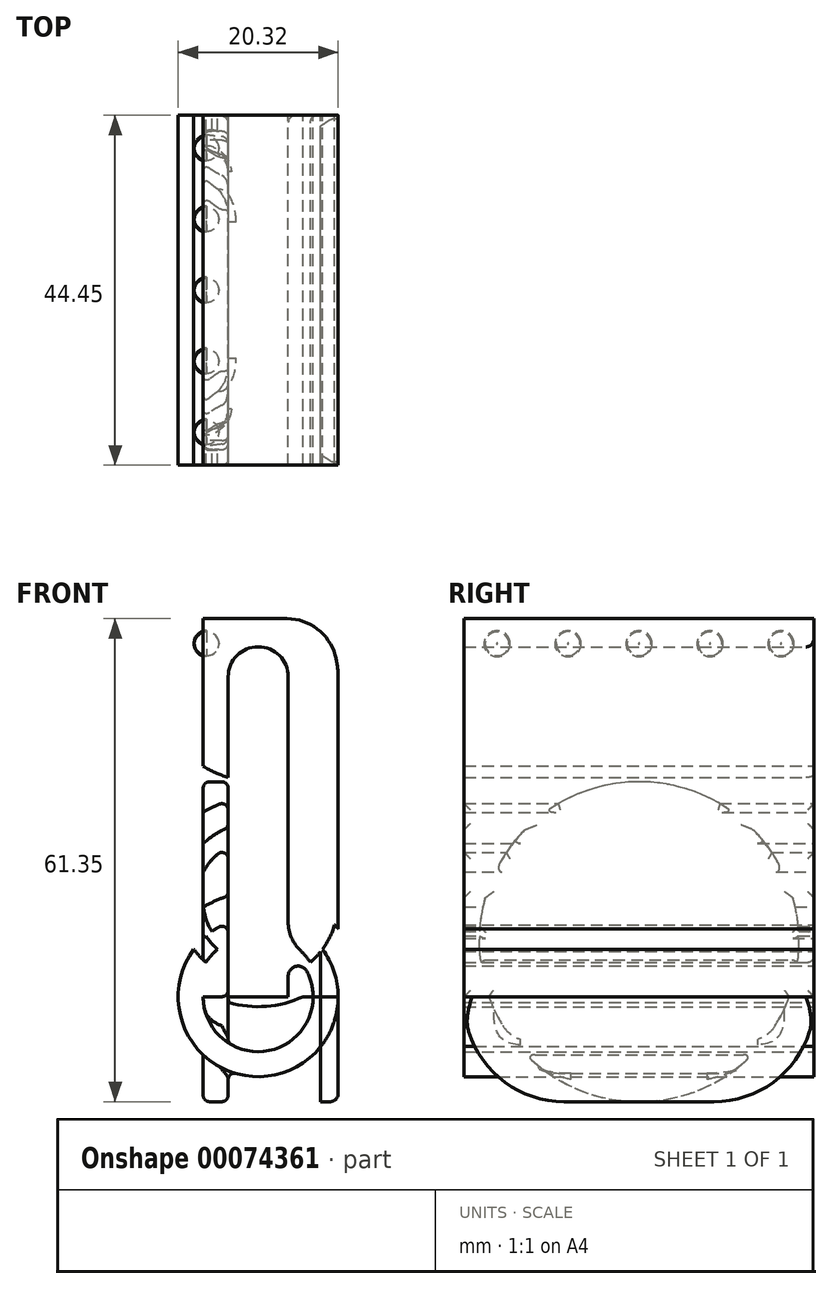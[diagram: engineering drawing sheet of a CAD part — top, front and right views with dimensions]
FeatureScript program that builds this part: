
annotation { "Feature Type Name" : "Feature", "Feature Type Description" : "" }
export const myFeature = defineFeature(function(context is Context, id is Id, definition is map)
    precondition{}
    {
        {
            var Q0;
            Q0=qCreatedBy(makeId("Front.planeOp"),FACE);
            var sketch = newSketch(context, id + "F0", { "sketchPlane" : qUnion([Q0])});
            skCircle(sketch, "E0", {"center": v(0, 0) * mm, "radius": 3.81 * mm});
            skCircle(sketch, "E1", {"center": v(0, -12.07) * mm, "radius": 3.81 * mm});
            skCircle(sketch, "E2", {"center": v(0, 0) * mm, "radius": 6.99 * mm});
            skCircle(sketch, "E3", {"center": v(0, -12.07) * mm, "radius": 6.99 * mm});
            skLineSegment(sketch, "E4", {"start": v(-6.99, -12.06) * mm, "end": v(-6.99, 28.58) * mm});
            skLineSegment(sketch, "E5", {"start": v(0, -12.07) * mm, "end": v(0, 0) * mm, "construction": true});
            skLineSegment(sketch, "E6", {"start": v(0, 0) * mm, "end": v(0, 28.58) * mm, "construction": true});
            skCircle(sketch, "E7", {"center": v(0, 28.58) * mm, "radius": 3.81 * mm});
            skCircle(sketch, "E8", {"center": v(0, 28.58) * mm, "radius": 10.16 * mm});
            skCircle(sketch, "E9", {"center": v(0, 0) * mm, "radius": 13.34 * mm});
            skCircle(sketch, "E10", {"center": v(0, -12.07) * mm, "radius": 13.34 * mm});
            skCircle(sketch, "E11", {"center": v(0, 28.58) * mm, "radius": 6.99 * mm});
            skCircle(sketch, "E12", {"center": v(0, 0) * mm, "radius": 7.94 * mm});
            skCircle(sketch, "E13", {"center": v(0, -12.07) * mm, "radius": 7.94 * mm});
            skCircle(sketch, "E14", {"center": v(0, 0) * mm, "radius": 10.16 * mm});
            skCircle(sketch, "E15", {"center": v(0, -12.07) * mm, "radius": 10.16 * mm});
            skCircle(sketch, "E16", {"center": v(0, 28.58) * mm, "radius": 13.34 * mm});
            skLineSegment(sketch, "E17", {"start": v(10.16, 28.58) * mm, "end": v(10.16, 0) * mm});
            skLineSegment(sketch, "E18", {"start": v(0, -25.4) * mm, "end": v(25.77, -25.4) * mm, "construction": true});
            skLineSegment(sketch, "E19", {"start": v(10.16, 0) * mm, "end": v(10.16, -25.4) * mm});
            skLineSegment(sketch, "E20", {"start": v(7.94, 0) * mm, "end": v(7.94, -25.4) * mm});
            skLineSegment(sketch, "E21", {"start": v(6.99, 28.58) * mm, "end": v(7.94, 0) * mm});
            skLineSegment(sketch, "E22", {"start": v(-6.99, 28.58) * mm, "end": v(10.16, 28.58) * mm});
            skLineSegment(sketch, "E23", {"start": v(-6.99, -12.07) * mm, "end": v(10.16, -12.07) * mm});
            skLineSegment(sketch, "E24", {"start": v(-3.81, 28.58) * mm, "end": v(-3.81, -12.07) * mm});
            skLineSegment(sketch, "E25", {"start": v(3.81, 28.58) * mm, "end": v(3.81, 0) * mm});
            skLineSegment(sketch, "E26", {"start": v(3.81, 0) * mm, "end": v(3.81, -12.07) * mm});
            skPoint(sketch, "E26.endSnap0", {"position": v(1.59, -12.07) * mm});
            skLineSegment(sketch, "E27", {"start": v(0, 0) * mm, "end": v(13.34, 0) * mm});
            skLineSegment(sketch, "E28", {"start": v(13.34, 0) * mm, "end": v(13.34, -25.4) * mm});
            skLineSegment(sketch, "E29", {"start": v(7.94, -25.4) * mm, "end": v(13.34, -25.4) * mm});
            skLineSegment(sketch, "E30", {"start": v(0, 41.91) * mm, "end": v(-27.15, 41.91) * mm, "construction": true});
            skLineSegment(sketch, "E31", {"start": v(-6.99, 28.58) * mm, "end": v(-6.99, 41.91) * mm});
            skLineSegment(sketch, "E32", {"start": v(-3.81, 28.58) * mm, "end": v(-3.81, 41.91) * mm});
            skCircle(sketch, "E33", {"center": v(0, 18.41) * mm, "radius": 3.81 * mm});
            skLineSegment(sketch, "E34", {"start": v(-6.99, 35.95) * mm, "end": v(19.22, 35.95) * mm});
            skSolve(sketch);
        }
        {
            var Q0;
            {var subQ1=sQuery(id+"F0.wireOp",EDGE,"E1");var subQ3=sQuery(id+"F0.wireOp",EDGE,"E9");var subQ4=makeQuery(id+"F0.imprint","INTERSECT",VERTEX,{"disambiguationData":[OD(1.0)],"derivedFrom":[subQ1,subQ3]});Q0=makeQuery(id+"F0.imprint","IMPRINT",FACE,{"disambiguationData":[TD([[makeQuery(id+"F0.imprint","IMPRINT",EDGE,{"disambiguationData":[TD([[subQ4,-1.0]])],"derivedFrom":subQ3}),1.0]])]});}
            var Q1;
            {var subQ0=sQuery(id+"F0.wireOp",EDGE,"E32");var subQ5=sQuery(id+"F0.wireOp",EDGE,"E11");var subQ6=makeQuery(id+"F0.imprint","INTERSECT",VERTEX,{"derivedFrom":[subQ5,subQ0]});Q1=makeQuery(id+"F0.imprint","IMPRINT",FACE,{"disambiguationData":[TD([[makeQuery(id+"F0.imprint","IMPRINT",EDGE,{"disambiguationData":[TD([[subQ6,1.0]])],"derivedFrom":subQ5}),1.0]])]});}
            var Q2;
            {var subQ1=sQuery(id+"F0.wireOp",EDGE,"E11");var subQ3=sQuery(id+"F0.wireOp",EDGE,"E24");var subQ4=makeQuery(id+"F0.imprint","INTERSECT",VERTEX,{"derivedFrom":[subQ1,subQ3]});Q2=makeQuery(id+"F0.imprint","IMPRINT",FACE,{"disambiguationData":[TD([[makeQuery(id+"F0.imprint","IMPRINT",EDGE,{"disambiguationData":[TD([[subQ4,1.0]])],"derivedFrom":subQ1}),1.0]])]});}
            var Q3;
            {var subQ1=sQuery(id+"F0.wireOp",EDGE,"E4");var subQ3=sQuery(id+"F0.wireOp",EDGE,"E8");var subQ4=makeQuery(id+"F0.imprint","INTERSECT",VERTEX,{"derivedFrom":[subQ1,subQ3]});Q3=makeQuery(id+"F0.imprint","IMPRINT",FACE,{"disambiguationData":[TD([[makeQuery(id+"F0.imprint","IMPRINT",EDGE,{"disambiguationData":[TD([[subQ4,-1.0]])],"derivedFrom":subQ3}),1.0]])]});}
            var Q4;
            {var subQ0=sQuery(id+"F0.wireOp",EDGE,"E16");var subQ1=sQuery(id+"F0.wireOp",EDGE,"E4");var subQ2=makeQuery(id+"F0.imprint","INTERSECT",VERTEX,{"derivedFrom":[subQ1,subQ0]});Q4=makeQuery(id+"F0.imprint","IMPRINT",FACE,{"disambiguationData":[TD([[makeQuery(id+"F0.imprint","IMPRINT",EDGE,{"disambiguationData":[TD([[subQ2,-1.0]])],"derivedFrom":subQ1}),-1.0]])]});}
            var Q5;
            {var subQ1=sQuery(id+"F0.wireOp",EDGE,"E3");var subQ7=sQuery(id+"F0.wireOp",EDGE,"E14");var subQ9=makeQuery(id+"F0.imprint","INTERSECT",VERTEX,{"disambiguationData":[OD(1.0)],"derivedFrom":[subQ1,subQ7]});Q5=makeQuery(id+"F0.imprint","IMPRINT",FACE,{"disambiguationData":[TD([[makeQuery(id+"F0.imprint","IMPRINT",EDGE,{"disambiguationData":[TD([[subQ9,-1.0]])],"derivedFrom":subQ1}),-1.0]])]});}
            var Q6;
            {var subQ1=sQuery(id+"F0.wireOp",EDGE,"E3");var subQ3=sQuery(id+"F0.wireOp",EDGE,"E9");var subQ4=makeQuery(id+"F0.imprint","INTERSECT",VERTEX,{"disambiguationData":[OD(1.0)],"derivedFrom":[subQ1,subQ3]});Q6=makeQuery(id+"F0.imprint","IMPRINT",FACE,{"disambiguationData":[TD([[makeQuery(id+"F0.imprint","IMPRINT",EDGE,{"disambiguationData":[TD([[subQ4,1.0]])],"derivedFrom":subQ3}),-1.0]])]});}
            var Q7;
            {var subQ0=sQuery(id+"F0.wireOp",EDGE,"E12");var subQ1=sQuery(id+"F0.wireOp",EDGE,"E4");var subQ2=makeQuery(id+"F0.imprint","INTERSECT",VERTEX,{"disambiguationData":[OD(1.0)],"derivedFrom":[subQ1,subQ0]});Q7=makeQuery(id+"F0.imprint","IMPRINT",FACE,{"disambiguationData":[TD([[makeQuery(id+"F0.imprint","IMPRINT",EDGE,{"disambiguationData":[TD([[subQ2,-1.0]])],"derivedFrom":subQ1}),-1.0]])]});}
            var Q8;
            {var subQ0=sQuery(id+"F0.wireOp",EDGE,"E24");var subQ1=sQuery(id+"F0.wireOp",EDGE,"E2");var subQ2=makeQuery(id+"F0.imprint","INTERSECT",VERTEX,{"disambiguationData":[OD(0.0)],"derivedFrom":[subQ1,subQ0]});Q8=makeQuery(id+"F0.imprint","IMPRINT",FACE,{"disambiguationData":[TD([[makeQuery(id+"F0.imprint","IMPRINT",EDGE,{"disambiguationData":[TD([[subQ2,-1.0]])],"derivedFrom":subQ1}),-1.0]])]});}
            var Q9;
            {var subQ0=sQuery(id+"F0.wireOp",EDGE,"E4");var subQ1=sQuery(id+"F0.wireOp",EDGE,"E2");var subQ2=makeQuery(id+"F0.imprint","INTERSECT",VERTEX,{"derivedFrom":[subQ1,subQ0]});Q9=makeQuery(id+"F0.imprint","IMPRINT",FACE,{"disambiguationData":[TD([[makeQuery(id+"F0.imprint","IMPRINT",EDGE,{"disambiguationData":[TD([[subQ2,-1.0]])],"derivedFrom":subQ1}),-1.0]])]});}
            var Q10;
            {var subQ0=sQuery(id+"F0.wireOp",EDGE,"E14");var subQ1=sQuery(id+"F0.wireOp",EDGE,"E4");var subQ2=makeQuery(id+"F0.imprint","INTERSECT",VERTEX,{"disambiguationData":[OD(0.0)],"derivedFrom":[subQ1,subQ0]});Q10=makeQuery(id+"F0.imprint","IMPRINT",FACE,{"disambiguationData":[TD([[makeQuery(id+"F0.imprint","IMPRINT",EDGE,{"disambiguationData":[TD([[subQ2,-1.0]])],"derivedFrom":subQ1}),-1.0]])]});}
            var Q11;
            {var subQ0=sQuery(id+"F0.wireOp",EDGE,"E9");var subQ1=sQuery(id+"F0.wireOp",EDGE,"E4");var subQ2=makeQuery(id+"F0.imprint","INTERSECT",VERTEX,{"disambiguationData":[OD(0.0)],"derivedFrom":[subQ1,subQ0]});Q11=makeQuery(id+"F0.imprint","IMPRINT",FACE,{"disambiguationData":[TD([[makeQuery(id+"F0.imprint","IMPRINT",EDGE,{"disambiguationData":[TD([[subQ2,-1.0]])],"derivedFrom":subQ1}),-1.0]])]});}
            var Q12;
            {var subQ0=sQuery(id+"F0.wireOp",EDGE,"E10");var subQ1=sQuery(id+"F0.wireOp",EDGE,"E2");var subQ2=makeQuery(id+"F0.imprint","INTERSECT",VERTEX,{"disambiguationData":[OD(0.0)],"derivedFrom":[subQ1,subQ0]});Q12=makeQuery(id+"F0.imprint","IMPRINT",FACE,{"disambiguationData":[TD([[makeQuery(id+"F0.imprint","IMPRINT",EDGE,{"disambiguationData":[TD([[subQ2,-1.0]])],"derivedFrom":subQ1}),-1.0]])]});}
            var Q13;
            {var subQ0=sQuery(id+"F0.wireOp",EDGE,"E13");var subQ1=sQuery(id+"F0.wireOp",EDGE,"E4");var subQ2=makeQuery(id+"F0.imprint","INTERSECT",VERTEX,{"derivedFrom":[subQ1,subQ0]});Q13=makeQuery(id+"F0.imprint","IMPRINT",FACE,{"disambiguationData":[TD([[makeQuery(id+"F0.imprint","IMPRINT",EDGE,{"disambiguationData":[TD([[subQ2,-1.0]])],"derivedFrom":subQ1}),-1.0]])]});}
            var Q14;
            {var subQ0=sQuery(id+"F0.wireOp",EDGE,"E24");var subQ1=sQuery(id+"F0.wireOp",EDGE,"E3");var subQ2=makeQuery(id+"F0.imprint","INTERSECT",VERTEX,{"derivedFrom":[subQ1,subQ0]});Q14=makeQuery(id+"F0.imprint","IMPRINT",FACE,{"disambiguationData":[TD([[makeQuery(id+"F0.imprint","IMPRINT",EDGE,{"disambiguationData":[TD([[subQ2,-1.0]])],"derivedFrom":subQ1}),1.0]])]});}
            var Q15;
            {var subQ0=sQuery(id+"F0.wireOp",EDGE,"E20");var subQ1=sQuery(id+"F0.wireOp",EDGE,"E10");var subQ2=makeQuery(id+"F0.imprint","INTERSECT",VERTEX,{"disambiguationData":[OD(0.0)],"derivedFrom":[subQ1,subQ0]});Q15=makeQuery(id+"F0.imprint","IMPRINT",FACE,{"disambiguationData":[TD([[makeQuery(id+"F0.imprint","IMPRINT",EDGE,{"disambiguationData":[TD([[subQ2,-1.0]])],"derivedFrom":subQ1}),1.0]])]});}
            var Q16;
            {var subQ1=sQuery(id+"F0.wireOp",EDGE,"E15");var subQ3=sQuery(id+"F0.wireOp",EDGE,"E20");var subQ4=makeQuery(id+"F0.imprint","INTERSECT",VERTEX,{"disambiguationData":[OD(1.0)],"derivedFrom":[subQ1,subQ3]});Q16=makeQuery(id+"F0.imprint","IMPRINT",FACE,{"disambiguationData":[TD([[makeQuery(id+"F0.imprint","IMPRINT",EDGE,{"disambiguationData":[TD([[subQ4,-1.0]])],"derivedFrom":subQ1}),1.0]])]});}
            var Q17;
            {var subQ0=sQuery(id+"F0.wireOp",EDGE,"E20");var subQ1=sQuery(id+"F0.wireOp",EDGE,"E14");var subQ2=makeQuery(id+"F0.imprint","INTERSECT",VERTEX,{"derivedFrom":[subQ1,subQ0]});Q17=makeQuery(id+"F0.imprint","IMPRINT",FACE,{"disambiguationData":[TD([[makeQuery(id+"F0.imprint","IMPRINT",EDGE,{"disambiguationData":[TD([[subQ2,-1.0]])],"derivedFrom":subQ1}),1.0]])]});}
            var Q18;
            {var subQ0=sQuery(id+"F0.wireOp",EDGE,"E15");var subQ1=sQuery(id+"F0.wireOp",EDGE,"E9");var subQ2=makeQuery(id+"F0.imprint","INTERSECT",VERTEX,{"disambiguationData":[OD(1.0)],"derivedFrom":[subQ1,subQ0]});Q18=makeQuery(id+"F0.imprint","IMPRINT",FACE,{"disambiguationData":[TD([[makeQuery(id+"F0.imprint","IMPRINT",EDGE,{"disambiguationData":[TD([[subQ2,-1.0]])],"derivedFrom":subQ1}),-1.0]])]});}
            var Q19;
            {var subQ3=sQuery(id+"F0.wireOp",EDGE,"E15");var subQ5=sQuery(id+"F0.wireOp",EDGE,"E9");var subQ6=makeQuery(id+"F0.imprint","INTERSECT",VERTEX,{"disambiguationData":[OD(1.0)],"derivedFrom":[subQ5,subQ3]});Q19=makeQuery(id+"F0.imprint","IMPRINT",FACE,{"disambiguationData":[TD([[makeQuery(id+"F0.imprint","IMPRINT",EDGE,{"disambiguationData":[TD([[subQ6,-1.0]])],"derivedFrom":subQ5}),1.0]])]});}
            var Q20;
            {var subQ1=sQuery(id+"F0.wireOp",EDGE,"E21");var subQ2=sQuery(id+"F0.wireOp",EDGE,"E12");var subQ4=makeQuery(id+"F0.imprint","INTERSECT",VERTEX,{"derivedFrom":[subQ2,subQ1]});Q20=makeQuery(id+"F0.imprint","IMPRINT",FACE,{"disambiguationData":[TD([[makeQuery(id+"F0.imprint","IMPRINT",EDGE,{"disambiguationData":[TD([[subQ4,1.0]])],"derivedFrom":subQ1}),1.0]])]});}
            var Q21;
            {var subQ0=sQuery(id+"F0.wireOp",EDGE,"E17");var subQ1=sQuery(id+"F0.wireOp",EDGE,"E9");var subQ2=makeQuery(id+"F0.imprint","INTERSECT",VERTEX,{"derivedFrom":[subQ1,subQ0]});Q21=makeQuery(id+"F0.imprint","IMPRINT",FACE,{"disambiguationData":[TD([[makeQuery(id+"F0.imprint","IMPRINT",EDGE,{"disambiguationData":[TD([[subQ2,-1.0]])],"derivedFrom":subQ1}),1.0]])]});}
            var Q22;
            {var subQ0=sQuery(id+"F0.wireOp",EDGE,"E17");var subQ1=sQuery(id+"F0.wireOp",EDGE,"E9");var subQ2=makeQuery(id+"F0.imprint","INTERSECT",VERTEX,{"derivedFrom":[subQ1,subQ0]});Q22=makeQuery(id+"F0.imprint","IMPRINT",FACE,{"disambiguationData":[TD([[makeQuery(id+"F0.imprint","IMPRINT",EDGE,{"disambiguationData":[TD([[subQ2,-1.0]])],"derivedFrom":subQ1}),-1.0]])]});}
            var Q23;
            {var subQ0=sQuery(id+"F0.wireOp",EDGE,"E17");var subQ5=sQuery(id+"F0.wireOp",EDGE,"E16");var subQ6=makeQuery(id+"F0.imprint","INTERSECT",VERTEX,{"derivedFrom":[subQ5,subQ0]});Q23=makeQuery(id+"F0.imprint","IMPRINT",FACE,{"disambiguationData":[TD([[makeQuery(id+"F0.imprint","IMPRINT",EDGE,{"disambiguationData":[TD([[subQ6,1.0]])],"derivedFrom":subQ5}),1.0]])]});}
            var Q24;
            {var subQ1=sQuery(id+"F0.wireOp",EDGE,"E8");var subQ3=sQuery(id+"F0.wireOp",EDGE,"E21");var subQ4=makeQuery(id+"F0.imprint","INTERSECT",VERTEX,{"derivedFrom":[subQ1,subQ3]});Q24=makeQuery(id+"F0.imprint","IMPRINT",FACE,{"disambiguationData":[TD([[makeQuery(id+"F0.imprint","IMPRINT",EDGE,{"disambiguationData":[TD([[subQ4,-1.0]])],"derivedFrom":subQ1}),1.0]])]});}
            var Q25;
            {var subQ1=sQuery(id+"F0.wireOp",EDGE,"E11");var subQ3=sQuery(id+"F0.wireOp",EDGE,"E25");var subQ4=makeQuery(id+"F0.imprint","INTERSECT",VERTEX,{"derivedFrom":[subQ1,subQ3]});Q25=makeQuery(id+"F0.imprint","IMPRINT",FACE,{"disambiguationData":[TD([[makeQuery(id+"F0.imprint","IMPRINT",EDGE,{"disambiguationData":[TD([[subQ4,-1.0]])],"derivedFrom":subQ1}),1.0]])]});}
            var Q26;
            {var subQ0=sQuery(id+"F0.wireOp",EDGE,"E25");var subQ1=sQuery(id+"F0.wireOp",EDGE,"E8");var subQ2=makeQuery(id+"F0.imprint","INTERSECT",VERTEX,{"derivedFrom":[subQ1,subQ0]});Q26=makeQuery(id+"F0.imprint","IMPRINT",FACE,{"disambiguationData":[TD([[makeQuery(id+"F0.imprint","IMPRINT",EDGE,{"disambiguationData":[TD([[subQ2,-1.0]])],"derivedFrom":subQ1}),1.0]])]});}
            var Q27;
            {var subQ0=sQuery(id+"F0.wireOp",EDGE,"E25");var subQ1=sQuery(id+"F0.wireOp",EDGE,"E8");var subQ2=makeQuery(id+"F0.imprint","INTERSECT",VERTEX,{"derivedFrom":[subQ1,subQ0]});Q27=makeQuery(id+"F0.imprint","IMPRINT",FACE,{"disambiguationData":[TD([[makeQuery(id+"F0.imprint","IMPRINT",EDGE,{"disambiguationData":[TD([[subQ2,-1.0]])],"derivedFrom":subQ1}),-1.0]])]});}
            var Q28;
            {var subQ0=sQuery(id+"F0.wireOp",EDGE,"E21");var subQ1=sQuery(id+"F0.wireOp",EDGE,"E9");var subQ2=makeQuery(id+"F0.imprint","INTERSECT",VERTEX,{"derivedFrom":[subQ1,subQ0]});Q28=makeQuery(id+"F0.imprint","IMPRINT",FACE,{"disambiguationData":[TD([[makeQuery(id+"F0.imprint","IMPRINT",EDGE,{"disambiguationData":[TD([[subQ2,-1.0]])],"derivedFrom":subQ1}),-1.0]])]});}
            var Q29;
            {var subQ0=sQuery(id+"F0.wireOp",EDGE,"E21");var subQ1=sQuery(id+"F0.wireOp",EDGE,"E9");var subQ2=makeQuery(id+"F0.imprint","INTERSECT",VERTEX,{"derivedFrom":[subQ1,subQ0]});Q29=makeQuery(id+"F0.imprint","IMPRINT",FACE,{"disambiguationData":[TD([[makeQuery(id+"F0.imprint","IMPRINT",EDGE,{"disambiguationData":[TD([[subQ2,-1.0]])],"derivedFrom":subQ1}),1.0]])]});}
            var Q30;
            {var subQ0=sQuery(id+"F0.wireOp",EDGE,"E21");var subQ1=sQuery(id+"F0.wireOp",EDGE,"E12");var subQ2=makeQuery(id+"F0.imprint","INTERSECT",VERTEX,{"derivedFrom":[subQ1,subQ0]});Q30=makeQuery(id+"F0.imprint","IMPRINT",FACE,{"disambiguationData":[TD([[makeQuery(id+"F0.imprint","IMPRINT",EDGE,{"disambiguationData":[TD([[subQ2,-1.0]])],"derivedFrom":subQ1}),-1.0]])]});}
            var Q31;
            {var subQ0=sQuery(id+"F0.wireOp",EDGE,"E14");var subQ1=sQuery(id+"F0.wireOp",EDGE,"E3");var subQ2=makeQuery(id+"F0.imprint","INTERSECT",VERTEX,{"disambiguationData":[OD(0.0)],"derivedFrom":[subQ1,subQ0]});Q31=makeQuery(id+"F0.imprint","IMPRINT",FACE,{"disambiguationData":[TD([[makeQuery(id+"F0.imprint","IMPRINT",EDGE,{"disambiguationData":[TD([[subQ2,-1.0]])],"derivedFrom":subQ1}),1.0]])]});}
            var Q32;
            {var subQ0=sQuery(id+"F0.wireOp",EDGE,"E20");var subQ1=sQuery(id+"F0.wireOp",EDGE,"E10");var subQ2=makeQuery(id+"F0.imprint","INTERSECT",VERTEX,{"disambiguationData":[OD(1.0)],"derivedFrom":[subQ1,subQ0]});Q32=makeQuery(id+"F0.imprint","IMPRINT",FACE,{"disambiguationData":[TD([[makeQuery(id+"F0.imprint","IMPRINT",EDGE,{"disambiguationData":[TD([[subQ2,-1.0]])],"derivedFrom":subQ1}),1.0]])]});}
            var Q33;
            {var subQ1=sQuery(id+"F0.wireOp",EDGE,"E12");var subQ6=sQuery(id+"F0.wireOp",EDGE,"E13");var subQ9=makeQuery(id+"F0.imprint","INTERSECT",VERTEX,{"disambiguationData":[OD(1.0)],"derivedFrom":[subQ1,subQ6]});Q33=makeQuery(id+"F0.imprint","IMPRINT",FACE,{"disambiguationData":[TD([[makeQuery(id+"F0.imprint","IMPRINT",EDGE,{"disambiguationData":[TD([[subQ9,-1.0]])],"derivedFrom":subQ1}),-1.0]])]});}
            var Q34;
            {var subQ0=sQuery(id+"F0.wireOp",EDGE,"E9");var subQ1=sQuery(id+"F0.wireOp",EDGE,"E1");var subQ7=makeQuery(id+"F0.imprint","INTERSECT",VERTEX,{"disambiguationData":[OD(0.0)],"derivedFrom":[subQ1,subQ0]});Q34=makeQuery(id+"F0.imprint","IMPRINT",FACE,{"disambiguationData":[TD([[makeQuery(id+"F0.imprint","IMPRINT",EDGE,{"disambiguationData":[TD([[subQ7,-1.0]])],"derivedFrom":subQ1}),-1.0]])]});}
            var Q35;
            {var subQ0=sQuery(id+"F0.wireOp",EDGE,"E25");var subQ1=sQuery(id+"F0.wireOp",EDGE,"E2");var subQ2=makeQuery(id+"F0.imprint","INTERSECT",VERTEX,{"derivedFrom":[subQ1,subQ0]});Q35=makeQuery(id+"F0.imprint","IMPRINT",FACE,{"disambiguationData":[TD([[makeQuery(id+"F0.imprint","IMPRINT",EDGE,{"disambiguationData":[TD([[subQ2,1.0]])],"derivedFrom":subQ1}),-1.0]])]});}
            var Q36;
            {var subQ0=sQuery(id+"F0.wireOp",EDGE,"E27");var subQ1=sQuery(id+"F0.wireOp",EDGE,"E2");var subQ2=makeQuery(id+"F0.imprint","INTERSECT",VERTEX,{"derivedFrom":[subQ1,subQ0]});Q36=makeQuery(id+"F0.imprint","IMPRINT",FACE,{"disambiguationData":[TD([[makeQuery(id+"F0.imprint","IMPRINT",EDGE,{"disambiguationData":[TD([[subQ2,1.0]])],"derivedFrom":subQ1}),-1.0]])]});}
            var Q37;
            {var subQ0=sQuery(id+"F0.wireOp",EDGE,"E27");var subQ1=sQuery(id+"F0.wireOp",EDGE,"E2");var subQ2=makeQuery(id+"F0.imprint","INTERSECT",VERTEX,{"derivedFrom":[subQ1,subQ0]});Q37=makeQuery(id+"F0.imprint","IMPRINT",FACE,{"disambiguationData":[TD([[makeQuery(id+"F0.imprint","IMPRINT",EDGE,{"disambiguationData":[TD([[subQ2,1.0]])],"derivedFrom":subQ1}),1.0]])]});}
            var Q38;
            {var subQ0=sQuery(id+"F0.wireOp",EDGE,"E20");var subQ1=sQuery(id+"F0.wireOp",EDGE,"E10");var subQ2=makeQuery(id+"F0.imprint","INTERSECT",VERTEX,{"disambiguationData":[OD(0.0)],"derivedFrom":[subQ1,subQ0]});Q38=makeQuery(id+"F0.imprint","IMPRINT",FACE,{"disambiguationData":[TD([[makeQuery(id+"F0.imprint","IMPRINT",EDGE,{"disambiguationData":[TD([[subQ2,-1.0]])],"derivedFrom":subQ1}),-1.0]])]});}
            var Q39;
            {var subQ1=sQuery(id+"F0.wireOp",EDGE,"E11");var subQ3=sQuery(id+"F0.wireOp",EDGE,"E32");var subQ4=makeQuery(id+"F0.imprint","INTERSECT",VERTEX,{"derivedFrom":[subQ1,subQ3]});Q39=makeQuery(id+"F0.imprint","IMPRINT",FACE,{"disambiguationData":[TD([[makeQuery(id+"F0.imprint","IMPRINT",EDGE,{"disambiguationData":[TD([[subQ4,-1.0]])],"derivedFrom":subQ1}),1.0]])]});}
            var Q40;
            {var subQ0=sQuery(id+"F0.wireOp",EDGE,"E21");var subQ1=sQuery(id+"F0.wireOp",EDGE,"E12");var subQ3=makeQuery(id+"F0.imprint","INTERSECT",VERTEX,{"derivedFrom":[subQ1,subQ0]});Q40=makeQuery(id+"F0.imprint","IMPRINT",FACE,{"disambiguationData":[TD([[makeQuery(id+"F0.imprint","IMPRINT",EDGE,{"disambiguationData":[TD([[subQ3,1.0]])],"derivedFrom":subQ1}),1.0]])]});}
            var Q41;
            {var subQ0=sQuery(id+"F0.wireOp",EDGE,"E14");var subQ1=sQuery(id+"F0.wireOp",EDGE,"E10");var subQ2=makeQuery(id+"F0.imprint","INTERSECT",VERTEX,{"disambiguationData":[OD(0.0)],"derivedFrom":[subQ1,subQ0]});Q41=makeQuery(id+"F0.imprint","IMPRINT",FACE,{"disambiguationData":[TD([[makeQuery(id+"F0.imprint","IMPRINT",EDGE,{"disambiguationData":[TD([[subQ2,-1.0]])],"derivedFrom":subQ1}),-1.0]])]});}
            var Q42;
            {var subQ0=sQuery(id+"F0.wireOp",EDGE,"E14");var subQ1=sQuery(id+"F0.wireOp",EDGE,"E10");var subQ2=makeQuery(id+"F0.imprint","INTERSECT",VERTEX,{"disambiguationData":[OD(0.0)],"derivedFrom":[subQ1,subQ0]});Q42=makeQuery(id+"F0.imprint","IMPRINT",FACE,{"disambiguationData":[TD([[makeQuery(id+"F0.imprint","IMPRINT",EDGE,{"disambiguationData":[TD([[subQ2,-1.0]])],"derivedFrom":subQ1}),1.0]])]});}
            var Q43;
            {var subQ0=sQuery(id+"F0.wireOp",EDGE,"E13");var subQ1=sQuery(id+"F0.wireOp",EDGE,"E2");var subQ2=makeQuery(id+"F0.imprint","INTERSECT",VERTEX,{"disambiguationData":[OD(1.0)],"derivedFrom":[subQ1,subQ0]});Q43=makeQuery(id+"F0.imprint","IMPRINT",FACE,{"disambiguationData":[TD([[makeQuery(id+"F0.imprint","IMPRINT",EDGE,{"disambiguationData":[TD([[subQ2,-1.0]])],"derivedFrom":subQ1}),-1.0]])]});}
            var Q44;
            {var subQ0=sQuery(id+"F0.wireOp",EDGE,"E13");var subQ1=sQuery(id+"F0.wireOp",EDGE,"E2");var subQ2=makeQuery(id+"F0.imprint","INTERSECT",VERTEX,{"disambiguationData":[OD(1.0)],"derivedFrom":[subQ1,subQ0]});Q44=makeQuery(id+"F0.imprint","IMPRINT",FACE,{"disambiguationData":[TD([[makeQuery(id+"F0.imprint","IMPRINT",EDGE,{"disambiguationData":[TD([[subQ2,-1.0]])],"derivedFrom":subQ1}),1.0]])]});}
            var Q45;
            {var subQ0=sQuery(id+"F0.wireOp",EDGE,"E13");var subQ1=sQuery(id+"F0.wireOp",EDGE,"E9");var subQ2=makeQuery(id+"F0.imprint","INTERSECT",VERTEX,{"disambiguationData":[OD(1.0)],"derivedFrom":[subQ1,subQ0]});Q45=makeQuery(id+"F0.imprint","IMPRINT",FACE,{"disambiguationData":[TD([[makeQuery(id+"F0.imprint","IMPRINT",EDGE,{"disambiguationData":[TD([[subQ2,-1.0]])],"derivedFrom":subQ1}),1.0]])]});}
            var Q46;
            {var subQ1=sQuery(id+"F0.wireOp",EDGE,"E3");var subQ7=sQuery(id+"F0.wireOp",EDGE,"E9");var subQ9=makeQuery(id+"F0.imprint","INTERSECT",VERTEX,{"disambiguationData":[OD(0.0)],"derivedFrom":[subQ1,subQ7]});Q46=makeQuery(id+"F0.imprint","IMPRINT",FACE,{"disambiguationData":[TD([[makeQuery(id+"F0.imprint","IMPRINT",EDGE,{"disambiguationData":[TD([[subQ9,-1.0]])],"derivedFrom":subQ1}),1.0]])]});}
            var Q47;
            {var subQ0=sQuery(id+"F0.wireOp",EDGE,"E9");var subQ1=sQuery(id+"F0.wireOp",EDGE,"E3");var subQ2=makeQuery(id+"F0.imprint","INTERSECT",VERTEX,{"disambiguationData":[OD(0.0)],"derivedFrom":[subQ1,subQ0]});Q47=makeQuery(id+"F0.imprint","IMPRINT",FACE,{"disambiguationData":[TD([[makeQuery(id+"F0.imprint","IMPRINT",EDGE,{"disambiguationData":[TD([[subQ2,1.0]])],"derivedFrom":subQ1}),1.0]])]});}
            var Q48;
            {var subQ5=sQuery(id+"F0.wireOp",EDGE,"E3");var subQ7=sQuery(id+"F0.wireOp",EDGE,"E14");var subQ8=makeQuery(id+"F0.imprint","INTERSECT",VERTEX,{"disambiguationData":[OD(1.0)],"derivedFrom":[subQ5,subQ7]});Q48=makeQuery(id+"F0.imprint","IMPRINT",FACE,{"disambiguationData":[TD([[makeQuery(id+"F0.imprint","IMPRINT",EDGE,{"disambiguationData":[TD([[subQ8,-1.0]])],"derivedFrom":subQ5}),1.0]])]});}
            var Q49;
            {var subQ0=sQuery(id+"F0.wireOp",EDGE,"E12");var subQ1=sQuery(id+"F0.wireOp",EDGE,"E3");var subQ2=makeQuery(id+"F0.imprint","INTERSECT",VERTEX,{"disambiguationData":[OD(1.0)],"derivedFrom":[subQ1,subQ0]});Q49=makeQuery(id+"F0.imprint","IMPRINT",FACE,{"disambiguationData":[TD([[makeQuery(id+"F0.imprint","IMPRINT",EDGE,{"disambiguationData":[TD([[subQ2,-1.0]])],"derivedFrom":subQ1}),1.0]])]});}
            var Q50;
            {var subQ0=sQuery(id+"F0.wireOp",EDGE,"E13");var subQ1=sQuery(id+"F0.wireOp",EDGE,"E2");var subQ2=makeQuery(id+"F0.imprint","INTERSECT",VERTEX,{"disambiguationData":[OD(0.0)],"derivedFrom":[subQ1,subQ0]});Q50=makeQuery(id+"F0.imprint","IMPRINT",FACE,{"disambiguationData":[TD([[makeQuery(id+"F0.imprint","IMPRINT",EDGE,{"disambiguationData":[TD([[subQ2,-1.0]])],"derivedFrom":subQ1}),-1.0]])]});}
            var Q51;
            {var subQ0=sQuery(id+"F0.wireOp",EDGE,"E13");var subQ1=sQuery(id+"F0.wireOp",EDGE,"E2");var subQ2=makeQuery(id+"F0.imprint","INTERSECT",VERTEX,{"disambiguationData":[OD(0.0)],"derivedFrom":[subQ1,subQ0]});Q51=makeQuery(id+"F0.imprint","IMPRINT",FACE,{"disambiguationData":[TD([[makeQuery(id+"F0.imprint","IMPRINT",EDGE,{"disambiguationData":[TD([[subQ2,-1.0]])],"derivedFrom":subQ1}),1.0]])]});}
            var Q52;
            {var subQ0=sQuery(id+"F0.wireOp",EDGE,"E15");var subQ1=sQuery(id+"F0.wireOp",EDGE,"E2");var subQ2=makeQuery(id+"F0.imprint","INTERSECT",VERTEX,{"disambiguationData":[OD(0.0)],"derivedFrom":[subQ1,subQ0]});Q52=makeQuery(id+"F0.imprint","IMPRINT",FACE,{"disambiguationData":[TD([[makeQuery(id+"F0.imprint","IMPRINT",EDGE,{"disambiguationData":[TD([[subQ2,-1.0]])],"derivedFrom":subQ1}),-1.0]])]});}
            var Q53;
            {var subQ0=sQuery(id+"F0.wireOp",EDGE,"E15");var subQ1=sQuery(id+"F0.wireOp",EDGE,"E2");var subQ2=makeQuery(id+"F0.imprint","INTERSECT",VERTEX,{"disambiguationData":[OD(0.0)],"derivedFrom":[subQ1,subQ0]});Q53=makeQuery(id+"F0.imprint","IMPRINT",FACE,{"disambiguationData":[TD([[makeQuery(id+"F0.imprint","IMPRINT",EDGE,{"disambiguationData":[TD([[subQ2,-1.0]])],"derivedFrom":subQ1}),1.0]])]});}
            var Q54;
            {var subQ0=sQuery(id+"F0.wireOp",EDGE,"E19");var subQ1=sQuery(id+"F0.wireOp",EDGE,"E10");var subQ2=makeQuery(id+"F0.imprint","INTERSECT",VERTEX,{"disambiguationData":[OD(0.0)],"derivedFrom":[subQ1,subQ0]});Q54=makeQuery(id+"F0.imprint","IMPRINT",FACE,{"disambiguationData":[TD([[makeQuery(id+"F0.imprint","IMPRINT",EDGE,{"disambiguationData":[TD([[subQ2,-1.0]])],"derivedFrom":subQ1}),-1.0]])]});}
            var Q55;
            {var subQ0=sQuery(id+"F0.wireOp",EDGE,"E9");var subQ1=sQuery(id+"F0.wireOp",EDGE,"E4");var subQ2=makeQuery(id+"F0.imprint","INTERSECT",VERTEX,{"disambiguationData":[OD(0.0)],"derivedFrom":[subQ1,subQ0]});Q55=makeQuery(id+"F0.imprint","IMPRINT",FACE,{"disambiguationData":[TD([[makeQuery(id+"F0.imprint","IMPRINT",EDGE,{"disambiguationData":[TD([[subQ2,1.0]])],"derivedFrom":subQ1}),-1.0]])]});}
            var Q56;
            {var subQ0=sQuery(id+"F0.wireOp",EDGE,"E15");var subQ1=sQuery(id+"F0.wireOp",EDGE,"E2");var subQ2=makeQuery(id+"F0.imprint","INTERSECT",VERTEX,{"disambiguationData":[OD(1.0)],"derivedFrom":[subQ1,subQ0]});Q56=makeQuery(id+"F0.imprint","IMPRINT",FACE,{"disambiguationData":[TD([[makeQuery(id+"F0.imprint","IMPRINT",EDGE,{"disambiguationData":[TD([[subQ2,-1.0]])],"derivedFrom":subQ1}),-1.0]])]});}
            var Q57;
            {var subQ0=sQuery(id+"F0.wireOp",EDGE,"E24");var subQ1=sQuery(id+"F0.wireOp",EDGE,"E2");var subQ2=makeQuery(id+"F0.imprint","INTERSECT",VERTEX,{"disambiguationData":[OD(0.0)],"derivedFrom":[subQ1,subQ0]});Q57=makeQuery(id+"F0.imprint","IMPRINT",FACE,{"disambiguationData":[TD([[makeQuery(id+"F0.imprint","IMPRINT",EDGE,{"disambiguationData":[TD([[subQ2,-1.0]])],"derivedFrom":subQ1}),1.0]])]});}
            var Q58;
            {var subQ0=sQuery(id+"F0.wireOp",EDGE,"E10");var subQ1=sQuery(id+"F0.wireOp",EDGE,"E2");var subQ2=makeQuery(id+"F0.imprint","INTERSECT",VERTEX,{"disambiguationData":[OD(0.0)],"derivedFrom":[subQ1,subQ0]});Q58=makeQuery(id+"F0.imprint","IMPRINT",FACE,{"disambiguationData":[TD([[makeQuery(id+"F0.imprint","IMPRINT",EDGE,{"disambiguationData":[TD([[subQ2,-1.0]])],"derivedFrom":subQ1}),1.0]])]});}
            var Q59;
            {var subQ0=sQuery(id+"F0.wireOp",EDGE,"E27");var subQ1=sQuery(id+"F0.wireOp",EDGE,"E10");var subQ2=makeQuery(id+"F0.imprint","INTERSECT",VERTEX,{"derivedFrom":[subQ1,subQ0]});Q59=makeQuery(id+"F0.imprint","IMPRINT",FACE,{"disambiguationData":[TD([[makeQuery(id+"F0.imprint","IMPRINT",EDGE,{"disambiguationData":[TD([[subQ2,-1.0]])],"derivedFrom":subQ1}),1.0]])]});}
            var Q60;
            {var subQ0=sQuery(id+"F0.wireOp",EDGE,"E25");var subQ1=sQuery(id+"F0.wireOp",EDGE,"E2");var subQ2=makeQuery(id+"F0.imprint","INTERSECT",VERTEX,{"derivedFrom":[subQ1,subQ0]});Q60=makeQuery(id+"F0.imprint","IMPRINT",FACE,{"disambiguationData":[TD([[makeQuery(id+"F0.imprint","IMPRINT",EDGE,{"disambiguationData":[TD([[subQ2,1.0]])],"derivedFrom":subQ1}),1.0]])]});}
            var Q61;
            {var subQ3=sQuery(id+"F0.wireOp",EDGE,"E15");var subQ5=sQuery(id+"F0.wireOp",EDGE,"E2");var subQ6=makeQuery(id+"F0.imprint","INTERSECT",VERTEX,{"disambiguationData":[OD(1.0)],"derivedFrom":[subQ5,subQ3]});Q61=makeQuery(id+"F0.imprint","IMPRINT",FACE,{"disambiguationData":[TD([[makeQuery(id+"F0.imprint","IMPRINT",EDGE,{"disambiguationData":[TD([[subQ6,-1.0]])],"derivedFrom":subQ5}),1.0]])]});}
            var Q62;
            {var subQ0=sQuery(id+"F0.wireOp",EDGE,"E12");var subQ1=sQuery(id+"F0.wireOp",EDGE,"E3");var subQ2=makeQuery(id+"F0.imprint","INTERSECT",VERTEX,{"disambiguationData":[OD(0.0)],"derivedFrom":[subQ1,subQ0]});Q62=makeQuery(id+"F0.imprint","IMPRINT",FACE,{"disambiguationData":[TD([[makeQuery(id+"F0.imprint","IMPRINT",EDGE,{"disambiguationData":[TD([[subQ2,-1.0]])],"derivedFrom":subQ1}),1.0]])]});}
            var Q63;
            {var subQ0=sQuery(id+"F0.wireOp",EDGE,"E20");var subQ1=sQuery(id+"F0.wireOp",EDGE,"E9");var subQ2=makeQuery(id+"F0.imprint","INTERSECT",VERTEX,{"derivedFrom":[subQ1,subQ0]});Q63=makeQuery(id+"F0.imprint","IMPRINT",FACE,{"disambiguationData":[TD([[makeQuery(id+"F0.imprint","IMPRINT",EDGE,{"disambiguationData":[TD([[subQ2,-1.0]])],"derivedFrom":subQ1}),-1.0]])]});}
            var Q64;
            {var subQ0=sQuery(id+"F0.wireOp",EDGE,"E20");var subQ1=sQuery(id+"F0.wireOp",EDGE,"E9");var subQ2=makeQuery(id+"F0.imprint","INTERSECT",VERTEX,{"derivedFrom":[subQ1,subQ0]});Q64=makeQuery(id+"F0.imprint","IMPRINT",FACE,{"disambiguationData":[TD([[makeQuery(id+"F0.imprint","IMPRINT",EDGE,{"disambiguationData":[TD([[subQ2,-1.0]])],"derivedFrom":subQ1}),1.0]])]});}
            var Q65;
            {var subQ0=sQuery(id+"F0.wireOp",EDGE,"E12");var subQ1=sQuery(id+"F0.wireOp",EDGE,"E3");var subQ2=makeQuery(id+"F0.imprint","INTERSECT",VERTEX,{"disambiguationData":[OD(1.0)],"derivedFrom":[subQ1,subQ0]});Q65=makeQuery(id+"F0.imprint","IMPRINT",FACE,{"disambiguationData":[TD([[makeQuery(id+"F0.imprint","IMPRINT",EDGE,{"disambiguationData":[TD([[subQ2,-1.0]])],"derivedFrom":subQ1}),-1.0]])]});}
            var Q66;
            {var subQ1=sQuery(id+"F0.wireOp",EDGE,"E1");var subQ3=sQuery(id+"F0.wireOp",EDGE,"E9");var subQ4=makeQuery(id+"F0.imprint","INTERSECT",VERTEX,{"disambiguationData":[OD(0.0)],"derivedFrom":[subQ1,subQ3]});Q66=makeQuery(id+"F0.imprint","IMPRINT",FACE,{"disambiguationData":[TD([[makeQuery(id+"F0.imprint","IMPRINT",EDGE,{"disambiguationData":[TD([[subQ4,1.0]])],"derivedFrom":subQ3}),1.0]])]});}
            var Q67;
            {var subQ1=sQuery(id+"F0.wireOp",EDGE,"E3");var subQ3=sQuery(id+"F0.wireOp",EDGE,"E9");var subQ4=makeQuery(id+"F0.imprint","INTERSECT",VERTEX,{"disambiguationData":[OD(1.0)],"derivedFrom":[subQ1,subQ3]});Q67=makeQuery(id+"F0.imprint","IMPRINT",FACE,{"disambiguationData":[TD([[makeQuery(id+"F0.imprint","IMPRINT",EDGE,{"disambiguationData":[TD([[subQ4,-1.0]])],"derivedFrom":subQ3}),-1.0]])]});}
            var Q68;
            {var subQ0=sQuery(id+"F0.wireOp",EDGE,"E15");var subQ1=sQuery(id+"F0.wireOp",EDGE,"E4");var subQ2=makeQuery(id+"F0.imprint","INTERSECT",VERTEX,{"derivedFrom":[subQ1,subQ0]});Q68=makeQuery(id+"F0.imprint","IMPRINT",FACE,{"disambiguationData":[TD([[makeQuery(id+"F0.imprint","IMPRINT",EDGE,{"disambiguationData":[TD([[subQ2,-1.0]])],"derivedFrom":subQ1}),-1.0]])]});}
            var Q69;
            {var subQ0=sQuery(id+"F0.wireOp",EDGE,"E20");var subQ1=sQuery(id+"F0.wireOp",EDGE,"E10");var subQ2=makeQuery(id+"F0.imprint","INTERSECT",VERTEX,{"disambiguationData":[OD(1.0)],"derivedFrom":[subQ1,subQ0]});Q69=makeQuery(id+"F0.imprint","IMPRINT",FACE,{"disambiguationData":[TD([[makeQuery(id+"F0.imprint","IMPRINT",EDGE,{"disambiguationData":[TD([[subQ2,-1.0]])],"derivedFrom":subQ1}),-1.0]])]});}
            var Q70;
            {var subQ0=sQuery(id+"F0.wireOp",EDGE,"E13");var subQ1=sQuery(id+"F0.wireOp",EDGE,"E9");var subQ2=makeQuery(id+"F0.imprint","INTERSECT",VERTEX,{"disambiguationData":[OD(1.0)],"derivedFrom":[subQ1,subQ0]});Q70=makeQuery(id+"F0.imprint","IMPRINT",FACE,{"disambiguationData":[TD([[makeQuery(id+"F0.imprint","IMPRINT",EDGE,{"disambiguationData":[TD([[subQ2,-1.0]])],"derivedFrom":subQ1}),-1.0]])]});}
            var Q71;
            {var subQ0=sQuery(id+"F0.wireOp",EDGE,"E32");var subQ1=sQuery(id+"F0.wireOp",EDGE,"E11");var subQ2=makeQuery(id+"F0.imprint","INTERSECT",VERTEX,{"derivedFrom":[subQ1,subQ0]});Q71=makeQuery(id+"F0.imprint","IMPRINT",FACE,{"disambiguationData":[TD([[makeQuery(id+"F0.imprint","IMPRINT",EDGE,{"disambiguationData":[TD([[subQ2,-1.0]])],"derivedFrom":subQ0}),-1.0]])]});}
            var Q72;
            {var subQ1=sQuery(id+"F0.wireOp",EDGE,"E11");var subQ3=sQuery(id+"F0.wireOp",EDGE,"E32");var subQ4=makeQuery(id+"F0.imprint","INTERSECT",VERTEX,{"derivedFrom":[subQ1,subQ3]});Q72=makeQuery(id+"F0.imprint","IMPRINT",FACE,{"disambiguationData":[TD([[makeQuery(id+"F0.imprint","IMPRINT",EDGE,{"disambiguationData":[TD([[subQ4,-1.0]])],"derivedFrom":subQ3}),1.0]])]});}
            extrude(context, id + "F1", {"entities" : qUnion([Q0, Q1, Q2, Q3, Q4, Q5, Q6, Q7, Q8, Q9, Q10, Q11, Q12, Q13, Q14, Q15, Q16, Q17, Q18, Q19, Q20, Q21, Q22, Q23, Q24, Q25, Q26, Q27, Q28, Q29, Q30, Q31, Q32, Q33, Q34, Q35, Q36, Q37, Q38, Q39, Q40, Q41, Q42, Q43, Q44, Q45, Q46, Q47, Q48, Q49, Q50, Q51, Q52, Q53, Q54, Q55, Q56, Q57, Q58, Q59, Q60, Q61, Q62, Q63, Q64, Q65, Q66, Q67, Q68, Q69, Q70, Q71, Q72]), "depth" : 44.45 * mm, "offsetDistance" : 25.4 * mm});
        }
        {
            var Q0;
            Q0=makeQuery(id+"F1.opExtrude","SWEPT_FACE",FACE,{"disambiguationData":[OSD([sQuery(id+"F0.wireOp",EDGE,"E4"),sQuery(id+"F0.wireOp",EDGE,"E31")])]});
            var sketch = newSketch(context, id + "F2", { "sketchPlane" : qUnion([Q0])});
            skLineSegment(sketch, "E35", {"start": v(22.23, 35.95) * mm, "end": v(22.23, -12.06) * mm, "construction": true});
            skLineSegment(sketch, "E36", {"start": v(0, 26.99) * mm, "end": v(44.45, 26.99) * mm, "construction": true});
            skLineSegment(sketch, "E37", {"start": v(0, -25.4) * mm, "end": v(44.45, -25.4) * mm, "construction": true});
            skPoint(sketch, "E37.endSnap0", {"position": v(44.45, 11.94) * mm});
            skCircle(sketch, "E38", {"center": v(22.23, -5.08) * mm, "radius": 20.32 * mm});
            skSolve(sketch);
        }
        {
            var Q0;
            Q0=makeQuery(id+"F1.opExtrude","SWEPT_EDGE",EDGE,{"disambiguationData":[OSD([sQuery(id+"F0.wireOp",EDGE,"E3"),sQuery(id+"F0.wireOp",EDGE,"E26")])]});
            fillet(context, id + "F3", {"entities" : qUnion([Q0]), "radius" : 1.27 * mm, "tangentPropagation" : true, "allowEdgeOverflow" : false});
        }
        {
            var Q0;
            {var subQ0=sQuery(id+"F2.wireOp",EDGE,"E38");var subQ1=makeQuery(id+"F1.opExtrude","SWEPT_EDGE",EDGE,{"disambiguationData":[OSD([sQuery(id+"F0.wireOp",EDGE,"E3"),sQuery(id+"F0.wireOp",EDGE,"E4"),sQuery(id+"F0.wireOp",EDGE,"E23")])]});var subQ2=makeQuery(id+"F2.imprint","INTERSECT",VERTEX,{"disambiguationData":[OD(0.0)],"derivedFrom":[subQ1,subQ0]});Q0=makeQuery(id+"F2.imprint","IMPRINT",FACE,{"disambiguationData":[TD([[makeQuery(id+"F2.imprint","IMPRINT",EDGE,{"disambiguationData":[TD([[subQ2,-1.0]])],"derivedFrom":subQ0}),1.0]])]});}
            extrude(context, id + "F4", {"entities" : qUnion([Q0]), "operationType" : NewBodyOperationType.ADD, "oppositeDirection" : true, "depth" : 3.17 * mm, "offsetDistance" : 25.4 * mm});
        }
        {
            var Q0;
            Q0=makeQuery(id+"F4.opExtrude","CAP_FACE",FACE,{"disambiguationData":[OSD([sQuery(id+"F0.wireOp",EDGE,"E3"),sQuery(id+"F0.wireOp",EDGE,"E4"),sQuery(id+"F0.wireOp",EDGE,"E23"),sQuery(id+"F2.wireOp",EDGE,"E38")])],"isStart":false});
            fillet(context, id + "F5", {"entities" : qUnion([Q0]), "radius" : 0.8 * mm, "tangentPropagation" : true, "allowEdgeOverflow" : false});
        }
        {
            var Q0;
            Q0=makeQuery(id+"F4.opExtrude","CAP_EDGE",EDGE,{"disambiguationData":[OSD([sQuery(id+"F2.wireOp",EDGE,"E38")])],"isStart":true});
            fillet(context, id + "F6", {"entities" : qUnion([Q0]), "radius" : 0.8 * mm, "tangentPropagation" : true, "allowEdgeOverflow" : false});
        }
        {
            var Q0;
            Q0=makeQuery(id+"F1.opExtrude","SWEPT_EDGE",EDGE,{"disambiguationData":[OSD([sQuery(id+"F0.wireOp",EDGE,"E13"),sQuery(id+"F0.wireOp",EDGE,"E26")])]});
            fillet(context, id + "F7", {"entities" : qUnion([Q0]), "radius" : 5.08 * mm, "tangentPropagation" : true, "allowEdgeOverflow" : false});
        }
        {
            var Q0;
            {var subQ0=sQuery(id+"F0.wireOp",EDGE,"E4");Q0=makeQuery(id+"F4.boolean.opBoolean","MERGE",FACE,{"derivedFrom":[makeQuery(id+"F1.opExtrude","SWEPT_FACE",FACE,{"disambiguationData":[OSD([subQ0,sQuery(id+"F0.wireOp",EDGE,"E31")])]}),makeQuery(id+"F4.opExtrude","CAP_FACE",FACE,{"disambiguationData":[OSD([sQuery(id+"F0.wireOp",EDGE,"E3"),subQ0,sQuery(id+"F0.wireOp",EDGE,"E23"),sQuery(id+"F2.wireOp",EDGE,"E38")])],"isStart":true})]});}
            var sketch = newSketch(context, id + "F8", { "sketchPlane" : qUnion([Q0])});
            skLineSegment(sketch, "E39", {"start": v(4.2, 35.95) * mm, "end": v(4.2, 23.25) * mm, "construction": true});
            skCircle(sketch, "E40", {"center": v(4.2, 32.78) * mm, "radius": 1.65 * mm});
            skLineSegment(sketch, "E41", {"start": v(0, 29.6) * mm, "end": v(44.45, 29.6) * mm, "construction": true});
            skPoint(sketch, "E41.startSnap0", {"position": v(4.2, 29.6) * mm});
            skCircle(sketch, "E42.MirrorC", {"center": v(4.2, 26.43) * mm, "radius": 1.65 * mm});
            skCircle(sketch, "E43.1.0.0", {"center": v(13.2, 32.78) * mm, "radius": 1.65 * mm});
            skCircle(sketch, "E43.1.0.1", {"center": v(13.2, 26.43) * mm, "radius": 1.65 * mm});
            skCircle(sketch, "E43.2.0.0", {"center": v(22.23, 32.78) * mm, "radius": 1.65 * mm});
            skCircle(sketch, "E43.2.0.1", {"center": v(22.23, 26.43) * mm, "radius": 1.65 * mm});
            skCircle(sketch, "E43.3.0.0", {"center": v(31.24, 32.78) * mm, "radius": 1.65 * mm});
            skCircle(sketch, "E43.3.0.1", {"center": v(31.24, 26.43) * mm, "radius": 1.65 * mm});
            skCircle(sketch, "E43.4.0.0", {"center": v(40.26, 32.78) * mm, "radius": 1.65 * mm});
            skCircle(sketch, "E43.4.0.1", {"center": v(40.26, 26.43) * mm, "radius": 1.65 * mm});
            skLineSegment(sketch, "E43.direction1", {"start": v(4.2, 32.78) * mm, "end": v(13.2, 32.78) * mm, "construction": true});
            skSolve(sketch);
        }
        {
            var Q0;
            Q0=makeQuery(id+"F8.imprint","IMPRINT",FACE,{"disambiguationData":[TD([[makeQuery(id+"F8.imprint","IMPRINT",EDGE,{"derivedFrom":sQuery(id+"F8.wireOp",EDGE,"E40")}),1.0]])]});
            var Q1;
            Q1=makeQuery(id+"F8.imprint","IMPRINT",FACE,{"disambiguationData":[TD([[makeQuery(id+"F8.imprint","IMPRINT",EDGE,{"derivedFrom":sQuery(id+"F8.wireOp",EDGE,"E42.MirrorC")}),-1.0]])]});
            var Q2;
            Q2=makeQuery(id+"F8.imprint","IMPRINT",FACE,{"disambiguationData":[TD([[makeQuery(id+"F8.imprint","IMPRINT",EDGE,{"derivedFrom":sQuery(id+"F8.wireOp",EDGE,"E43.1.0.0")}),1.0]])]});
            var Q3;
            Q3=makeQuery(id+"F8.imprint","IMPRINT",FACE,{"disambiguationData":[TD([[makeQuery(id+"F8.imprint","IMPRINT",EDGE,{"derivedFrom":sQuery(id+"F8.wireOp",EDGE,"E43.1.0.1")}),-1.0]])]});
            var Q4;
            Q4=makeQuery(id+"F8.imprint","IMPRINT",FACE,{"disambiguationData":[TD([[makeQuery(id+"F8.imprint","IMPRINT",EDGE,{"derivedFrom":sQuery(id+"F8.wireOp",EDGE,"E43.2.0.1")}),-1.0]])]});
            var Q5;
            Q5=makeQuery(id+"F8.imprint","IMPRINT",FACE,{"disambiguationData":[TD([[makeQuery(id+"F8.imprint","IMPRINT",EDGE,{"derivedFrom":sQuery(id+"F8.wireOp",EDGE,"E43.2.0.0")}),1.0]])]});
            var Q6;
            Q6=makeQuery(id+"F8.imprint","IMPRINT",FACE,{"disambiguationData":[TD([[makeQuery(id+"F8.imprint","IMPRINT",EDGE,{"derivedFrom":sQuery(id+"F8.wireOp",EDGE,"E43.3.0.0")}),1.0]])]});
            var Q7;
            Q7=makeQuery(id+"F8.imprint","IMPRINT",FACE,{"disambiguationData":[TD([[makeQuery(id+"F8.imprint","IMPRINT",EDGE,{"derivedFrom":sQuery(id+"F8.wireOp",EDGE,"E43.3.0.1")}),-1.0]])]});
            var Q8;
            Q8=makeQuery(id+"F8.imprint","IMPRINT",FACE,{"disambiguationData":[TD([[makeQuery(id+"F8.imprint","IMPRINT",EDGE,{"derivedFrom":sQuery(id+"F8.wireOp",EDGE,"E43.4.0.1")}),-1.0]])]});
            var Q9;
            Q9=makeQuery(id+"F8.imprint","IMPRINT",FACE,{"disambiguationData":[TD([[makeQuery(id+"F8.imprint","IMPRINT",EDGE,{"derivedFrom":sQuery(id+"F8.wireOp",EDGE,"E43.4.0.0")}),1.0]])]});
            extrude(context, id + "F9", {"entities" : qUnion([Q0, Q1, Q2, Q3, Q4, Q5, Q6, Q7, Q8, Q9]), "operationType" : NewBodyOperationType.REMOVE, "oppositeDirection" : true, "depth" : 2.03 * mm, "offsetDistance" : 25.4 * mm});
        }
        {
            var Q0;
            Q0=makeQuery(id+"F9.boolean.opBoolean","COPY",EDGE,{"derivedFrom":makeQuery(id+"F9.opExtrude","CAP_EDGE",EDGE,{"disambiguationData":[OSD([sQuery(id+"F8.wireOp",EDGE,"E40")])],"isStart":false})});
            var Q1;
            Q1=makeQuery(id+"F9.boolean.opBoolean","COPY",EDGE,{"derivedFrom":makeQuery(id+"F9.opExtrude","CAP_EDGE",EDGE,{"disambiguationData":[OSD([sQuery(id+"F8.wireOp",EDGE,"E42.MirrorC")])],"isStart":false})});
            var Q2;
            Q2=makeQuery(id+"F9.boolean.opBoolean","COPY",EDGE,{"derivedFrom":makeQuery(id+"F9.opExtrude","CAP_EDGE",EDGE,{"disambiguationData":[OSD([sQuery(id+"F8.wireOp",EDGE,"E43.1.0.0")])],"isStart":false})});
            var Q3;
            Q3=makeQuery(id+"F9.boolean.opBoolean","COPY",EDGE,{"derivedFrom":makeQuery(id+"F9.opExtrude","CAP_EDGE",EDGE,{"disambiguationData":[OSD([sQuery(id+"F8.wireOp",EDGE,"E43.1.0.1")])],"isStart":false})});
            var Q4;
            Q4=makeQuery(id+"F9.boolean.opBoolean","COPY",EDGE,{"derivedFrom":makeQuery(id+"F9.opExtrude","CAP_EDGE",EDGE,{"disambiguationData":[OSD([sQuery(id+"F8.wireOp",EDGE,"E43.2.0.0")])],"isStart":false})});
            var Q5;
            Q5=makeQuery(id+"F9.boolean.opBoolean","COPY",EDGE,{"derivedFrom":makeQuery(id+"F9.opExtrude","CAP_EDGE",EDGE,{"disambiguationData":[OSD([sQuery(id+"F8.wireOp",EDGE,"E43.2.0.1")])],"isStart":false})});
            var Q6;
            Q6=makeQuery(id+"F9.boolean.opBoolean","COPY",EDGE,{"derivedFrom":makeQuery(id+"F9.opExtrude","CAP_EDGE",EDGE,{"disambiguationData":[OSD([sQuery(id+"F8.wireOp",EDGE,"E43.3.0.0")])],"isStart":false})});
            var Q7;
            Q7=makeQuery(id+"F9.boolean.opBoolean","COPY",EDGE,{"derivedFrom":makeQuery(id+"F9.opExtrude","CAP_EDGE",EDGE,{"disambiguationData":[OSD([sQuery(id+"F8.wireOp",EDGE,"E43.3.0.1")])],"isStart":false})});
            var Q8;
            Q8=makeQuery(id+"F9.boolean.opBoolean","COPY",FACE,{"derivedFrom":makeQuery(id+"F9.opExtrude","CAP_FACE",FACE,{"disambiguationData":[OSD([sQuery(id+"F8.wireOp",EDGE,"E43.4.0.1")])],"isStart":false})});
            var Q9;
            Q9=makeQuery(id+"F9.boolean.opBoolean","COPY",EDGE,{"derivedFrom":makeQuery(id+"F9.opExtrude","CAP_EDGE",EDGE,{"disambiguationData":[OSD([sQuery(id+"F8.wireOp",EDGE,"E43.4.0.0")])],"isStart":false})});
            fillet(context, id + "F10", {"entities" : qUnion([Q0, Q1, Q2, Q3, Q4, Q5, Q6, Q7, Q8, Q9]), "radius" : 1.59 * mm, "tangentPropagation" : true, "allowEdgeOverflow" : false});
        }
        {
            var Q0;
            Q0=makeQuery(id+"F1.opExtrude","SWEPT_EDGE",EDGE,{"disambiguationData":[OSD([sQuery(id+"F0.wireOp",EDGE,"E8"),sQuery(id+"F0.wireOp",EDGE,"E34")])]});
            fillet(context, id + "F11", {"entities" : qUnion([Q0]), "radius" : 6.35 * mm, "tangentPropagation" : true, "allowEdgeOverflow" : false});
        }
        {
            var Q0;
            Q0=makeQuery(id+"F1.opExtrude","CAP_EDGE",EDGE,{"disambiguationData":[OSD([sQuery(id+"F0.wireOp",EDGE,"E29")])],"isStart":true});
            var Q1;
            Q1=makeQuery(id+"F1.opExtrude","CAP_EDGE",EDGE,{"disambiguationData":[OSD([sQuery(id+"F0.wireOp",EDGE,"E29")])],"isStart":false});
            fillet(context, id + "F12", {"entities" : qUnion([Q0, Q1]), "radius" : 12.7 * mm, "tangentPropagation" : true, "allowEdgeOverflow" : false});
        }
        {
            var Q0;
            Q0=makeQuery(id+"F1.opExtrude","SWEPT_EDGE",EDGE,{"disambiguationData":[OSD([sQuery(id+"F0.wireOp",EDGE,"E19"),sQuery(id+"F0.wireOp",EDGE,"E29")])]});
            var Q1;
            Q1=makeQuery(id+"F1.opExtrude","CAP_EDGE",EDGE,{"disambiguationData":[OSD([sQuery(id+"F0.wireOp",EDGE,"E24")])],"isStart":true});
            fillet(context, id + "F13", {"entities" : qUnion([Q0, Q1]), "radius" : 1.02 * mm, "tangentPropagation" : true, "allowEdgeOverflow" : false});
        }
    });
